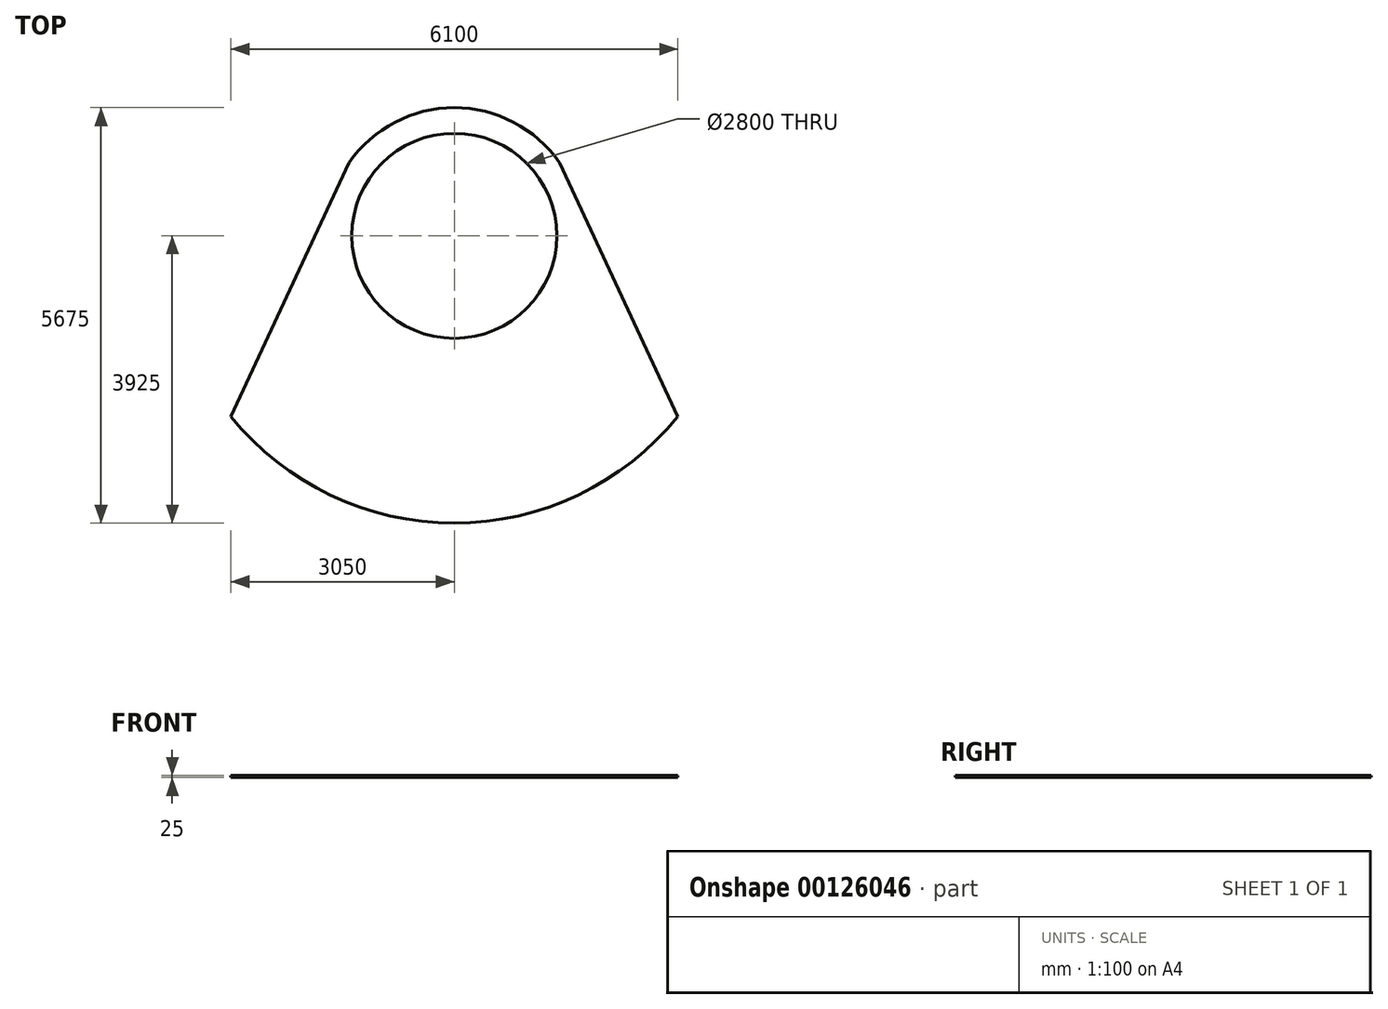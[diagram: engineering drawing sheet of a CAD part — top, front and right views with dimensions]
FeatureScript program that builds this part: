
annotation { "Feature Type Name" : "Feature", "Feature Type Description" : "" }
export const myFeature = defineFeature(function(context is Context, id is Id, definition is map)
    precondition{}
    {
        {
            var Q0;
            Q0=qCreatedBy(makeId("Top.planeOp"),FACE);
            var sketch = newSketch(context, id + "F0", { "sketchPlane" : qUnion([Q0])});
            skCircle(sketch, "E0", {"center": v(0, 0) * mm, "radius": 1400 * mm});
            skArc(sketch, "E1", {"start": v(1436.14, 1000) * mm, "mid": v(0, 1750) * mm, "end": v(-1436.14, 1000) * mm});
            skArc(sketch, "E2", {"start": v(-3050, -2470.45) * mm, "mid": v(0, -3925) * mm, "end": v(3050, -2470.45) * mm});
            skLineSegment(sketch, "E3", {"start": v(-1436.14, 1000) * mm, "end": v(-3050, -2470.45) * mm});
            skLineSegment(sketch, "E4", {"start": v(1436.14, 1000) * mm, "end": v(3050, -2470.45) * mm});
            skPoint(sketch, "E5", {"position": v(-850, -2470.45) * mm});
            skPoint(sketch, "E6", {"position": v(850, -2470.45) * mm});
            skSolve(sketch);
        }
        {
            var Q0;
            Q0=makeQuery(id+"F0.imprint","IMPRINT",FACE,{"disambiguationData":[TD([[makeQuery(id+"F0.imprint","IMPRINT",EDGE,{"derivedFrom":sQuery(id+"F0.wireOp",EDGE,"E0")}),-1.0]])]});
            extrude(context, id + "F1", {"entities" : qUnion([Q0]), "depth" : 25 * mm});
        }
    });
